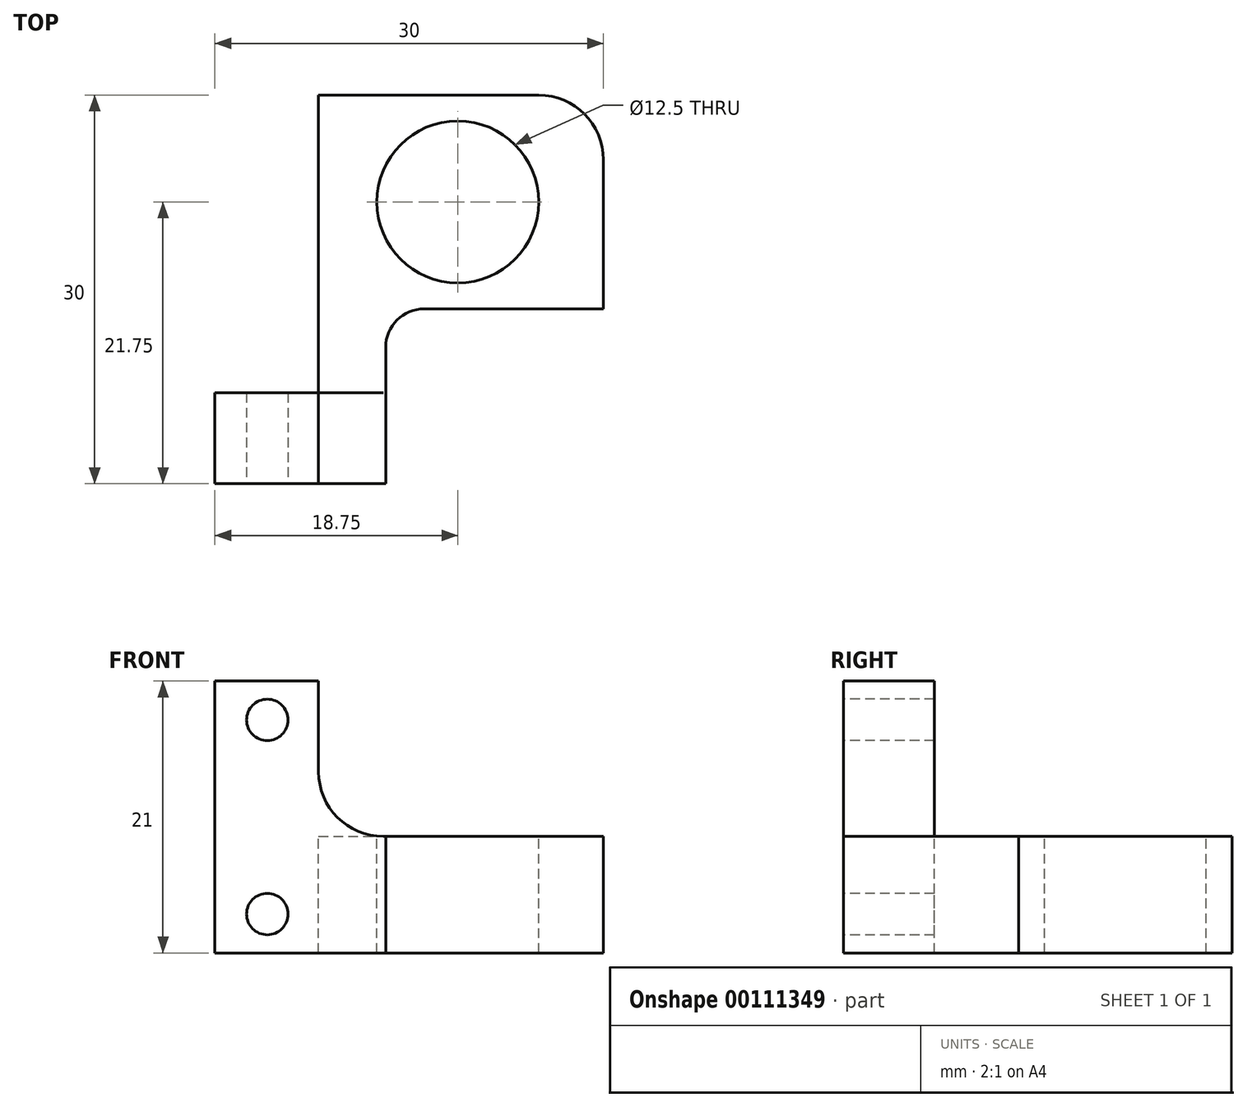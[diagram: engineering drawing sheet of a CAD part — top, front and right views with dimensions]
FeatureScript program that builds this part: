
annotation { "Feature Type Name" : "Feature", "Feature Type Description" : "" }
export const myFeature = defineFeature(function(context is Context, id is Id, definition is map)
    precondition{}
    {
        {
            var Q0;
            Q0=qCreatedBy(makeId("Top.planeOp"),FACE);
            var sketch = newSketch(context, id + "F0", { "sketchPlane" : qUnion([Q0])});
            skLineSegment(sketch, "E0.bottom", {"start": v(0, 0) * mm, "end": v(28, 0) * mm});
            skLineSegment(sketch, "E0.top", {"start": v(0, 30) * mm, "end": v(28, 30) * mm});
            skLineSegment(sketch, "E0.left", {"start": v(0, 0) * mm, "end": v(0, 30) * mm});
            skLineSegment(sketch, "E0.right", {"start": v(28, 0) * mm, "end": v(28, 30) * mm});
            skSolve(sketch);
        }
        {
            var Q0;
            Q0=qSketchRegion(id+"F0",true);
            extrude(context, id + "F1", {"entities" : qUnion([Q0]), "depth" : 4 * mm});
        }
        {
            var Q0;
            Q0=makeQuery(id+"F1.opExtrude","CAP_FACE",FACE,{"disambiguationData":[OSD([sQuery(id+"F0.wireOp",EDGE,"E0.bottom"),sQuery(id+"F0.wireOp",EDGE,"E0.top"),sQuery(id+"F0.wireOp",EDGE,"E0.left"),sQuery(id+"F0.wireOp",EDGE,"E0.right")])],"isStart":false});
            var sketch = newSketch(context, id + "F2", { "sketchPlane" : qUnion([Q0])});
            skCircle(sketch, "E1", {"center": v(16.75, 21.75) * mm, "radius": 6.25 * mm});
            skLineSegment(sketch, "E2.bottom", {"start": v(0, 30) * mm, "end": v(6, 30) * mm});
            skLineSegment(sketch, "E2.top", {"start": v(0, 7) * mm, "end": v(6, 7) * mm});
            skLineSegment(sketch, "E2.left", {"start": v(0, 30) * mm, "end": v(0, 7) * mm});
            skLineSegment(sketch, "E2.right", {"start": v(6, 30) * mm, "end": v(6, 7) * mm});
            skLineSegment(sketch, "E3.bottom", {"start": v(28, 0) * mm, "end": v(11.18, 0) * mm});
            skLineSegment(sketch, "E3.top", {"start": v(28, 13.5) * mm, "end": v(11.18, 13.5) * mm});
            skLineSegment(sketch, "E3.left", {"start": v(28, 0) * mm, "end": v(28, 13.5) * mm});
            skLineSegment(sketch, "E3.right", {"start": v(11.18, 0) * mm, "end": v(11.18, 13.5) * mm});
            skSolve(sketch);
        }
        {
            var Q0;
            Q0=qSketchRegion(id+"F2",true);
            extrude(context, id + "F3", {"entities" : qUnion([Q0]), "operationType" : NewBodyOperationType.REMOVE, "oppositeDirection" : true, "depth" : 25 * mm});
        }
        {
            var Q0;
            Q0=makeQuery(id+"F1.opExtrude","CAP_FACE",FACE,{"disambiguationData":[OSD([sQuery(id+"F0.wireOp",EDGE,"E0.bottom"),sQuery(id+"F0.wireOp",EDGE,"E0.top"),sQuery(id+"F0.wireOp",EDGE,"E0.left"),sQuery(id+"F0.wireOp",EDGE,"E0.right")])],"isStart":false});
            var sketch = newSketch(context, id + "F4", { "sketchPlane" : qUnion([Q0])});
            skLineSegment(sketch, "E4.bottom", {"start": v(0, 7) * mm, "end": v(6, 7) * mm});
            skLineSegment(sketch, "E4.top", {"start": v(0, 0) * mm, "end": v(6, 0) * mm});
            skLineSegment(sketch, "E4.left", {"start": v(0, 7) * mm, "end": v(0, 0) * mm});
            skLineSegment(sketch, "E4.right", {"start": v(6, 7) * mm, "end": v(6, 0) * mm});
            skSolve(sketch);
        }
        {
            var Q0;
            Q0=qSketchRegion(id+"F4",true);
            var Q1;
            {var subQ1=sQuery(id+"F4.wireOp",EDGE,"E4.right");Q1=makeQuery(id+"F4.imprint","IMPRINT",FACE,{"disambiguationData":[TD([[makeQuery(id+"F4.imprint","IMPRINT",EDGE,{"derivedFrom":subQ1}),1.0]])]});}
            extrude(context, id + "F5", {"entities" : qUnion([Q0, Q1]), "operationType" : NewBodyOperationType.ADD, "depth" : 5 * mm, "offsetDistance" : 25 * mm});
        }
        {
            var Q0;
            Q0=makeQuery(id+"F4.imprint","IMPRINT",FACE,{"disambiguationData":[TD([[makeQuery(id+"F4.imprint","IMPRINT",EDGE,{"derivedFrom":sQuery(id+"F4.wireOp",EDGE,"E4.bottom")}),-1.0]])]});
            extrude(context, id + "F6", {"entities" : qUnion([Q0]), "operationType" : NewBodyOperationType.ADD, "depth" : 17 * mm});
        }
        {
            var Q0;
            Q0=makeQuery(id+"F5.boolean.opBoolean","MERGE",FACE,{"derivedFrom":[makeQuery(id+"F1.opExtrude","SWEPT_FACE",FACE,{"disambiguationData":[OSD([sQuery(id+"F0.wireOp",EDGE,"E0.bottom")])]}),makeQuery(id+"F5.opExtrude","SWEPT_FACE",FACE,{"disambiguationData":[OSD([sQuery(id+"F4.wireOp",EDGE,"E4.top")])]})]});
            var sketch = newSketch(context, id + "F7", { "sketchPlane" : qUnion([Q0])});
            skLineSegment(sketch, "E5", {"start": v(2.04, 18) * mm, "end": v(2.04, 3) * mm});
            skCircle(sketch, "E6", {"center": v(2.04, 18) * mm, "radius": 1.6 * mm});
            skCircle(sketch, "E7", {"center": v(2.04, 3) * mm, "radius": 1.6 * mm});
            skSolve(sketch);
        }
        {
            var Q0;
            Q0=qSketchRegion(id+"F7",true);
            extrude(context, id + "F8", {"entities" : qUnion([Q0]), "operationType" : NewBodyOperationType.REMOVE, "oppositeDirection" : true, "depth" : 25 * mm});
        }
        {
            var Q0;
            Q0=makeQuery(id+"F1.opExtrude","SWEPT_EDGE",EDGE,{"disambiguationData":[OSD([sQuery(id+"F0.wireOp",EDGE,"E0.bottom"),sQuery(id+"F0.wireOp",EDGE,"E0.right")])]});
            var Q1;
            Q1=makeQuery(id+"F1.opExtrude","SWEPT_EDGE",EDGE,{"disambiguationData":[OSD([sQuery(id+"F0.wireOp",EDGE,"E0.top"),sQuery(id+"F0.wireOp",EDGE,"E0.right")])]});
            var Q2;
            Q2=makeQuery(id+"F3.boolean.opBoolean","COPY",EDGE,{"derivedFrom":makeQuery(id+"F3.opExtrude","SWEPT_EDGE",EDGE,{"disambiguationData":[OSD([sQuery(id+"F0.wireOp",EDGE,"E0.top"),sQuery(id+"F2.wireOp",EDGE,"E2.bottom"),sQuery(id+"F2.wireOp",EDGE,"E2.right")])]})});
            var Q3;
            Q3=makeQuery(id+"F3.boolean.opBoolean","COPY",EDGE,{"derivedFrom":makeQuery(id+"F3.opExtrude","SWEPT_EDGE",EDGE,{"disambiguationData":[OSD([sQuery(id+"F0.wireOp",EDGE,"E0.right"),sQuery(id+"F2.wireOp",EDGE,"E3.top"),sQuery(id+"F2.wireOp",EDGE,"E3.left")])]})});
            fillet(context, id + "F9", {"entities" : qUnion([Q0, Q1, Q2, Q3]), "radius" : 5 * mm, "tangentPropagation" : true, "allowEdgeOverflow" : false});
        }
        {
            var Q0;
            {var subQ0=sQuery(id+"F2.wireOp",EDGE,"E3.top");var subQ1=sQuery(id+"F2.wireOp",EDGE,"E3.right");Q0=makeQuery(id+"F5.boolean.opBoolean","MERGE",EDGE,{"derivedFrom":[makeQuery(id+"F3.boolean.opBoolean","COPY",EDGE,{"derivedFrom":makeQuery(id+"F3.opExtrude","SWEPT_EDGE",EDGE,{"disambiguationData":[OSD([subQ0,subQ1])]})}),makeQuery(id+"F5.opExtrude","SWEPT_EDGE",EDGE,{"disambiguationData":[OSD([subQ0,subQ1])]})]});}
            fillet(context, id + "F10", {"entities" : qUnion([Q0]), "radius" : 3 * mm, "tangentPropagation" : true, "allowEdgeOverflow" : false});
        }
        {
            var Q0;
            Q0=makeQuery(id+"F6.boolean.opBoolean","INTERSECT",EDGE,{"derivedFrom":[makeQuery(id+"F5.opExtrude","CAP_FACE",FACE,{"disambiguationData":[OSD([sQuery(id+"F0.wireOp",EDGE,"E0.bottom"),sQuery(id+"F0.wireOp",EDGE,"E0.top"),sQuery(id+"F0.wireOp",EDGE,"E0.right"),sQuery(id+"F2.wireOp",EDGE,"E1"),sQuery(id+"F2.wireOp",EDGE,"E2.right"),sQuery(id+"F2.wireOp",EDGE,"E3.top"),sQuery(id+"F2.wireOp",EDGE,"E3.right"),sQuery(id+"F4.wireOp",EDGE,"E4.bottom"),sQuery(id+"F4.wireOp",EDGE,"E4.top"),sQuery(id+"F4.wireOp",EDGE,"E4.left")])],"isStart":false}),makeQuery(id+"F6.opExtrude","SWEPT_FACE",FACE,{"disambiguationData":[OSD([sQuery(id+"F4.wireOp",EDGE,"E4.right")])]})]});
            fillet(context, id + "F11", {"entities" : qUnion([Q0]), "radius" : 5 * mm, "tangentPropagation" : true, "allowEdgeOverflow" : false});
        }
        {
            var Q0;
            {var subQ0=sQuery(id+"F4.wireOp",EDGE,"E4.left");Q0=makeQuery(id+"F6.boolean.opBoolean","MERGE",FACE,{"derivedFrom":[makeQuery(id+"F5.boolean.opBoolean","MERGE",FACE,{"derivedFrom":[makeQuery(id+"F1.opExtrude","SWEPT_FACE",FACE,{"disambiguationData":[OSD([sQuery(id+"F0.wireOp",EDGE,"E0.left")])]}),makeQuery(id+"F5.opExtrude","SWEPT_FACE",FACE,{"disambiguationData":[OSD([subQ0])]})]}),makeQuery(id+"F6.opExtrude","SWEPT_FACE",FACE,{"disambiguationData":[OSD([subQ0])]})]});}
            extrude(context, id + "F12", {"entities" : qUnion([Q0]), "operationType" : NewBodyOperationType.ADD, "depth" : 2 * mm, "offsetDistance" : 25 * mm});
        }
    });
